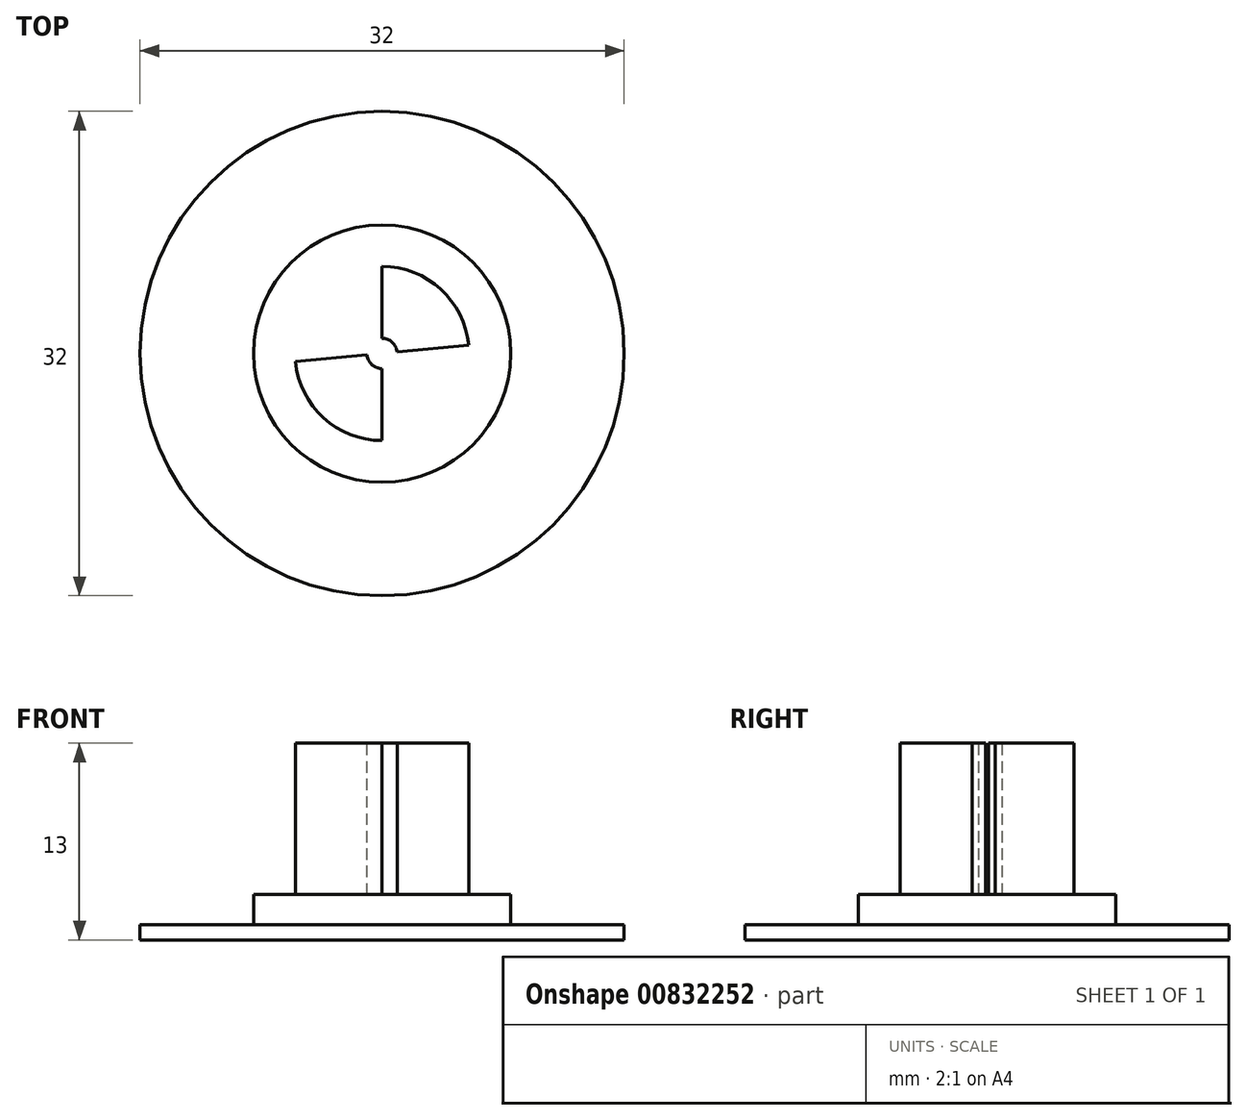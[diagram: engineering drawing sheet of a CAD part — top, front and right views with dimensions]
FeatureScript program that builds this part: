
annotation { "Feature Type Name" : "Feature", "Feature Type Description" : "" }
export const myFeature = defineFeature(function(context is Context, id is Id, definition is map)
    precondition{}
    {
        {
            var Q0;
            Q0=qCreatedBy(makeId("Top.planeOp"),FACE);
            var sketch = newSketch(context, id + "F0", { "sketchPlane" : qUnion([Q0])});
            skCircle(sketch, "E0", {"center": v(0, 0) * mm, "radius": 16 * mm});
            skSolve(sketch);
        }
        {
            var Q0;
            Q0=makeQuery(id+"F0.imprint","IMPRINT",FACE,{"disambiguationData":[TD([[makeQuery(id+"F0.imprint","IMPRINT",EDGE,{"derivedFrom":sQuery(id+"F0.wireOp",EDGE,"E0")}),1.0]])]});
            extrude(context, id + "F1", {"entities" : qUnion([Q0]), "depth" : 1 * mm, "offsetDistance" : 25 * mm});
        }
        {
            var Q0;
            Q0=makeQuery(id+"F1.opExtrude","CAP_FACE",FACE,{"disambiguationData":[OSD([sQuery(id+"F0.wireOp",EDGE,"E0")])],"isStart":false});
            var sketch = newSketch(context, id + "F2", { "sketchPlane" : qUnion([Q0])});
            skCircle(sketch, "E1", {"center": v(0, 0) * mm, "radius": 8.5 * mm});
            skSolve(sketch);
        }
        {
            var Q0;
            Q0=makeQuery(id+"F2.imprint","IMPRINT",FACE,{"disambiguationData":[TD([[makeQuery(id+"F2.imprint","IMPRINT",EDGE,{"derivedFrom":sQuery(id+"F2.wireOp",EDGE,"E1")}),1.0]])]});
            extrude(context, id + "F3", {"entities" : qUnion([Q0]), "operationType" : NewBodyOperationType.ADD, "depth" : 2 * mm, "offsetDistance" : 25 * mm});
        }
        {
            var Q0;
            Q0=makeQuery(id+"F3.opExtrude","CAP_FACE",FACE,{"disambiguationData":[OSD([sQuery(id+"F2.wireOp",EDGE,"E1")])],"isStart":false});
            var sketch = newSketch(context, id + "F4", { "sketchPlane" : qUnion([Q0])});
            skCircle(sketch, "E2", {"center": v(0, 0) * mm, "radius": 5.75 * mm});
            skSolve(sketch);
        }
        {
            var Q0;
            Q0=makeQuery(id+"F4.imprint","IMPRINT",FACE,{"disambiguationData":[TD([[makeQuery(id+"F4.imprint","IMPRINT",EDGE,{"derivedFrom":sQuery(id+"F4.wireOp",EDGE,"E2")}),1.0]])]});
            extrude(context, id + "F5", {"entities" : qUnion([Q0]), "operationType" : NewBodyOperationType.ADD, "depth" : 10 * mm, "offsetDistance" : 25 * mm});
        }
        {
            var Q0;
            Q0=makeQuery(id+"F5.opExtrude","CAP_FACE",FACE,{"disambiguationData":[OSD([sQuery(id+"F4.wireOp",EDGE,"E2")])],"isStart":false});
            var sketch = newSketch(context, id + "F6", { "sketchPlane" : qUnion([Q0])});
            skArc(sketch, "E3", {"start": v(0, 5.75) * mm, "mid": v(-4.25, 3.87) * mm, "end": v(-5.73, -0.53) * mm});
            skLineSegment(sketch, "E4", {"start": v(-1, -0.1) * mm, "end": v(-5.73, -0.53) * mm});
            skLineSegment(sketch, "E5", {"start": v(0, 1) * mm, "end": v(0, 5.75) * mm});
            skLineSegment(sketch, "E6", {"start": v(0, -1) * mm, "end": v(0, -5.75) * mm});
            skLineSegment(sketch, "E7", {"start": v(-5.73, -0.53) * mm, "end": v(-1, -0.1) * mm});
            skArc(sketch, "E8", {"start": v(0, -5.75) * mm, "mid": v(4.25, -3.87) * mm, "end": v(5.73, 0.53) * mm});
            skArc(sketch, "E9", {"start": v(1, 0.1) * mm, "mid": v(0.67, 0.74) * mm, "end": v(0, 1) * mm});
            skPoint(sketch, "E10", {"position": v(-1, -0.1) * mm});
            skPoint(sketch, "E11", {"position": v(0, -1) * mm});
            skPoint(sketch, "E12", {"position": v(0, 1) * mm});
            skPoint(sketch, "E13", {"position": v(1, 0.1) * mm});
            skLineSegment(sketch, "E14.trimOffspring", {"start": v(1, 0.1) * mm, "end": v(5.73, 0.53) * mm});
            skArc(sketch, "E15.trimOffspring", {"start": v(-1, -0.1) * mm, "mid": v(-0.67, -0.74) * mm, "end": v(0, -1) * mm});
            skSolve(sketch);
        }
        {
            var Q0;
            Q0 = qSketchRegion(id + "F6", true);
            extrude(context, id + "F7", {"entities" : qUnion([Q0]), "operationType" : NewBodyOperationType.REMOVE, "oppositeDirection" : true, "depth" : 10 * mm, "offsetDistance" : 25 * mm});
        }
    });
